# Revit family: Ustroystvo distantsionnogo puska vzryvozashchishchennoe UDP 535-Ekhd «MOROZ»
name_source: partatom
category: Пожарная сигнализация
units: mm (PartAtom-declared; Revit-internal decimal feet)

## family parameters
Всегда вертикально = Да
Заголовок OmniClass = Communication and Data Processing Equipment
На основе рабочей плоскости = Нет
Номер OmniClass = 23.85.50.17
Общий = Нет
При загрузке вырезать с полостями = Нет
Размер круглого соединителя = Использовать диаметр
Сохранять ориентацию аннотаций = Нет
Тип детали = Нормальный
Точка принадлежности помещению = Нет

## types (1)
- УСТРОЙСТВО ДИСТАНЦИОННОГО ПУСКА ВЗРЫВОЗАЩИЩЁННОЕ УДП 535-ЕХD «МОРОЗ»
    ADSK_Единица измерения = шт.
    ADSK_Завод-изготовитель = ООО НПП «МАГНИТО-КОНТАКТ»
    ADSK_Материал = Сплав алюминевый
    ADSK_Наименование = Устройство дистанционного пуска взрывозащищённое УДП 535-Ехd «МОРОЗ»
    ADSK_Наименование краткое = УДП 535-Ехd «МОРОЗ»
    ADSK_Обозначение = АТФЕ.425211.001ПС
    ADSK_Примечание = Устройства дистанционного пуска УДП 535-Ехd «МОРОЗ» должны применяться с кабельными вводами МКВ или Ех МКВМ (см. таблицу) и Ех-заглушками завода-изготовителя или другими кабельными вводами и заглушками, соответствующими требованиям ТР ТС 012/2011, имеющими действующий сертификат соответствия, обеспечивающими вид и уровень взрывозащиты, а так же степень защиты оболочки, соответствующие УДП 535-Ехd «МОРОЗ». Материал уплотнительных колец должен быть рассчитан на работу при температуре окружающей среды, соответствующей условиям эксплуатации устройства.
    ADSK_Размер_Высота = 110 мм
    ADSK_Размер_Диаметр = 6 мм
    ADSK_Размер_Длина = 210 мм
    URL = https://m-kontakt.ru
    Диапазон рабочих температур = -60°С ... + 70°С (Т6); -60°С ... + 95°С (Т5)
    Заглушка = Да
    Звено цепочки = Да
    Изготовитель = ООО НПП «МАГНИТО-КОНТАКТ»
    Искробезопасные параметры = Ui - 30 B,Ii - 100 мA,Pi - 1 Вт,Li - 10 мкГн,Ci - 50 пФ
    Кабельный ввод = Да
    Класс по степени защиты = III по ГОСТ 12.2.007.0
    Левый кабельный ввод = Да
    Максимально допустимая влажность = 98%
    Наклейка = Наклейка
    Напряжение питания = 9 - 30 В
    Описание = Устройство дистанционного пуска взрывозащищённое УДП 535-Ехd «МОРОЗ» с маркировкой взрывозащиты 1Ex db IIC T6…T5 Db / Ex tb IIIC T85°C…T100°C Db / Ex ia IIIC T85°C…T100°C Da (в дальнейшем устройство) предназначено для запуска систем пожарной автоматики, систем дымоудаления, формирования аварийных сигналов или сигналов для разблокирования аварийных выходов при включении магнитоконтактного приводного элемента.
    Отметка по умолчанию = 0 мм
    Правый кабельный ввод = Да
    Пружинный шплинт = Да
    Светопропуск = Светопропуск
    Средний потребляемый ток = не более 50 мкА
    Степень зашиты корпуса = IP66
    Ток потребления в режиме "Пожар" = 10±2 мА (при 9 В), не более 20±2 мА (при 30 В)
